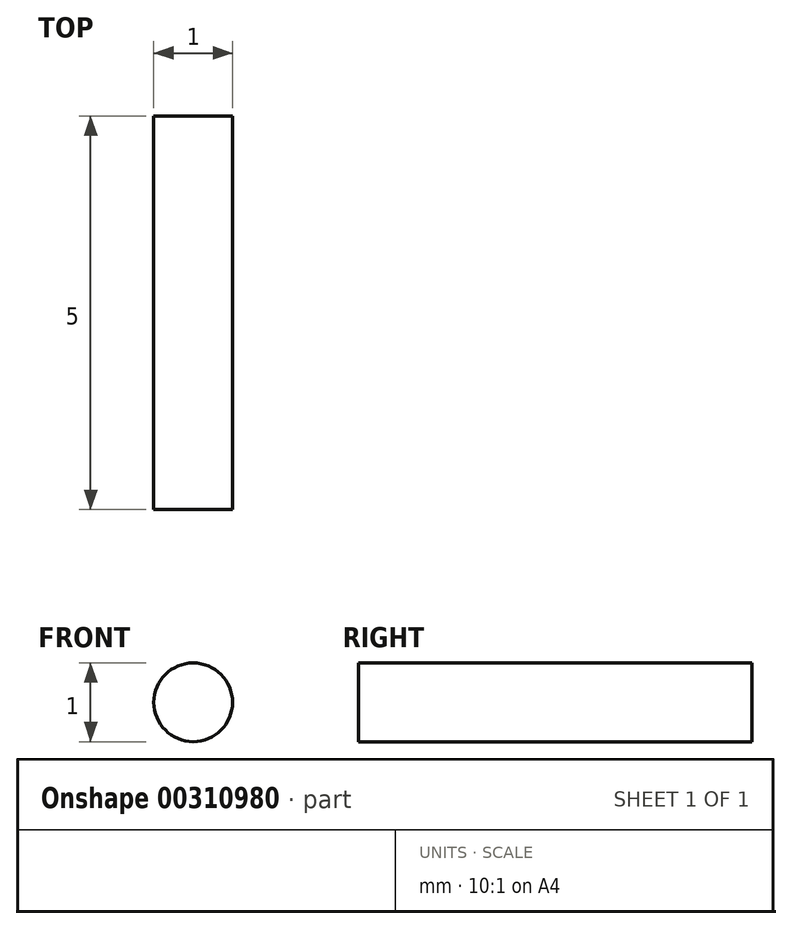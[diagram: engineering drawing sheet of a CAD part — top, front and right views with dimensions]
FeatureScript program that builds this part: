
annotation { "Feature Type Name" : "Feature", "Feature Type Description" : "" }
export const myFeature = defineFeature(function(context is Context, id is Id, definition is map)
    precondition{}
    {
        {
            var Q0;
            Q0=qCreatedBy(makeId("Front.planeOp"),FACE);
            var sketch = newSketch(context, id + "F0", { "sketchPlane" : qUnion([Q0])});
            skCircle(sketch, "E0", {"center": v(0, 0) * mm, "radius": 0.5 * mm});
            skSolve(sketch);
        }
        {
            var Q0;
            Q0=makeQuery(id+"F0.imprint","IMPRINT",FACE,{"disambiguationData":[TD([[makeQuery(id+"F0.imprint","IMPRINT",EDGE,{"derivedFrom":sQuery(id+"F0.wireOp",EDGE,"E0")}),1.0]])]});
            extrude(context, id + "F1", {"entities" : qUnion([Q0]), "depth" : 5 * mm});
        }
    });
